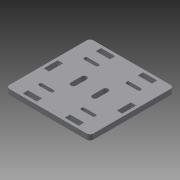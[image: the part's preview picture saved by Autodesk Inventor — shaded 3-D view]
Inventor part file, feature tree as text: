
AUTODESK INVENTOR PART (.ipt)
format: ipt  version: 2015 SP1 (Build 190203100, 203)  size: 162,816 bytes
history: native  units: in
note: dims shown in document units (in); Inventor stores cm internally (conversion verified against a paired STEP export)
features: extrude x2, sketch x2, fillet x1
ambient origin geometry x8: Origin, YZ Plane, XZ Plane, XY Plane, X Axis, Y Axis, Z Axis, Center Point
bodies: Solid1 (feature_tree)
feature tree (5):
  extrude  "Extrusion1"  Depth=3.0in
  extrude  "Extrusion3"  Depth=0.19in
  fillet  "Fillet1"  Radius=0.1in
  sketch  "Sketch1"  dims[d0=3.0in d1=3.0in]
  sketch  "Sketch3"  dims[d2=0.5in d3=0.19in d4=0.1in d5=0.5in d6=1.25in d7=0.1in d8=0.19in d9=0.5in d10=0.19in d11=0.0in d12=0.125in d13=0.125in d16=0.1875in d17=0.1875in d18=0.19in d19=0.0in d20=0.125in]
